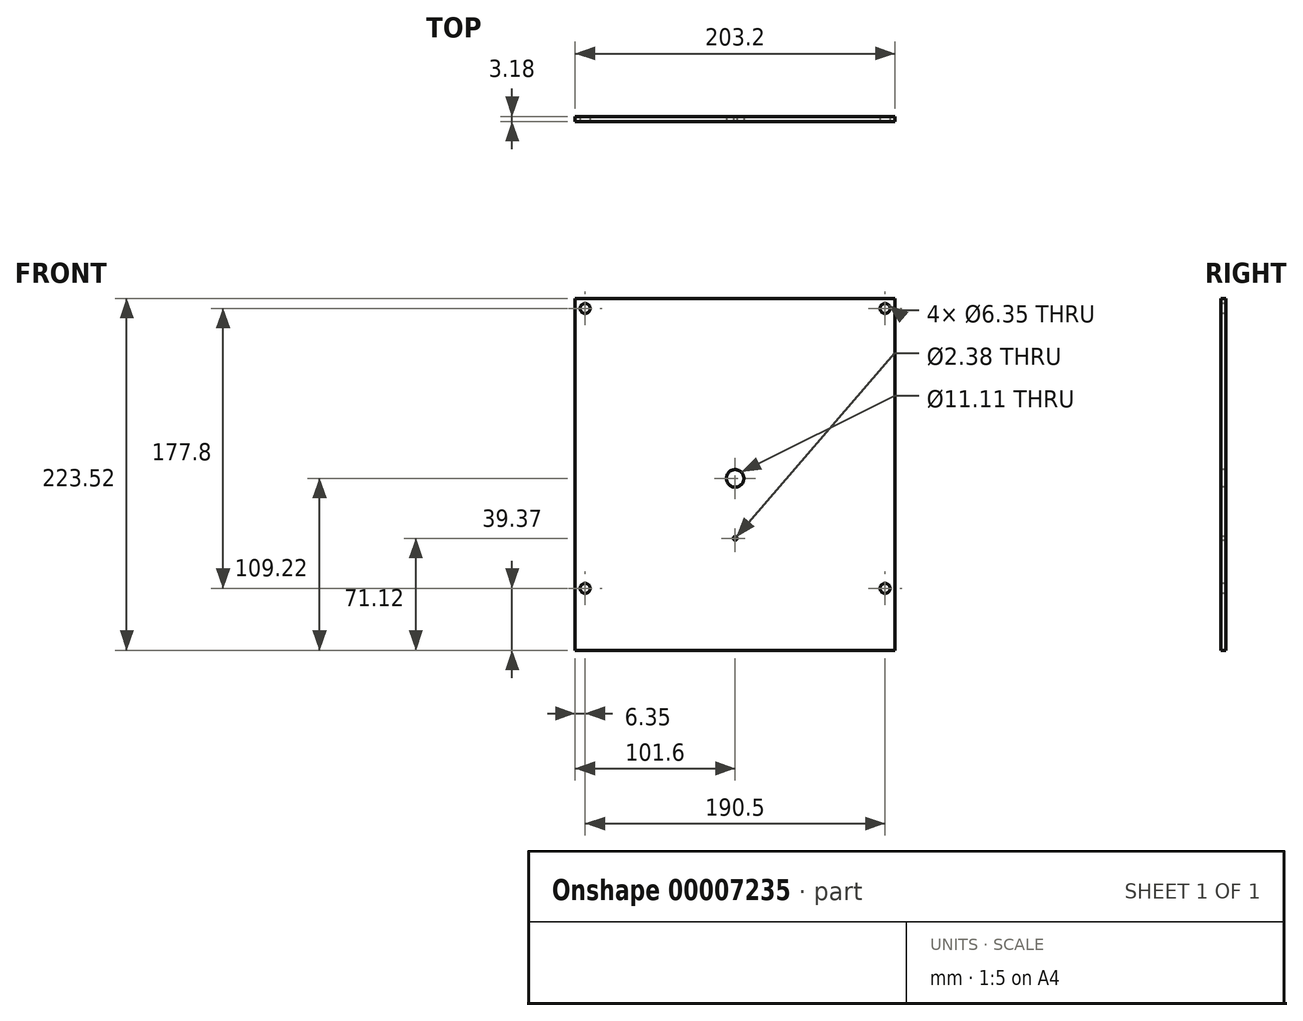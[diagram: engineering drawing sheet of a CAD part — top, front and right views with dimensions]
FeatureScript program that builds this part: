
annotation { "Feature Type Name" : "Feature", "Feature Type Description" : "" }
export const myFeature = defineFeature(function(context is Context, id is Id, definition is map)
    precondition{}
    {
        {
            var Q0;
            Q0=qCreatedBy(makeId("Front.planeOp"),FACE);
            var sketch = newSketch(context, id + "F0", { "sketchPlane" : qUnion([Q0])});
            skLineSegment(sketch, "E0.bottom", {"start": v(-101.6, 114.3) * mm, "end": v(101.6, 114.3) * mm});
            skLineSegment(sketch, "E0.top", {"start": v(-101.6, -109.22) * mm, "end": v(101.6, -109.22) * mm});
            skLineSegment(sketch, "E0.left", {"start": v(-101.6, 114.3) * mm, "end": v(-101.6, -109.22) * mm});
            skLineSegment(sketch, "E0.right", {"start": v(101.6, 114.3) * mm, "end": v(101.6, -109.22) * mm});
            skLineSegment(sketch, "E1", {"start": v(0, -109.22) * mm, "end": v(0, 114.3) * mm, "construction": true});
            skSolve(sketch);
        }
        {
            var Q0;
            Q0=qSketchRegion(id+"F0",true);
            extrude(context, id + "F1", {"entities" : qUnion([Q0]), "oppositeDirection" : true, "depth" : 3.17 * mm});
        }
        {
            var Q0;
            Q0=makeQuery(id+"F1.opExtrude","CAP_FACE",FACE,{"disambiguationData":[OSD([sQuery(id+"F0.wireOp",EDGE,"E0.bottom"),sQuery(id+"F0.wireOp",EDGE,"E0.top"),sQuery(id+"F0.wireOp",EDGE,"E0.left"),sQuery(id+"F0.wireOp",EDGE,"E0.right")])],"isStart":true});
            var sketch = newSketch(context, id + "F2", { "sketchPlane" : qUnion([Q0])});
            skCircle(sketch, "E2", {"center": v(0, 0) * mm, "radius": 5.56 * mm});
            skCircle(sketch, "E3", {"center": v(0, -38.1) * mm, "radius": 1.2 * mm});
            skSolve(sketch);
        }
        {
            var Q0;
            Q0=qSketchRegion(id+"F2",true);
            extrude(context, id + "F3", {"entities" : qUnion([Q0]), "operationType" : NewBodyOperationType.REMOVE, "oppositeDirection" : true, "depth" : 25.4 * mm});
        }
        {
            var Q0;
            Q0=makeQuery(id+"F1.opExtrude","CAP_FACE",FACE,{"disambiguationData":[OSD([sQuery(id+"F0.wireOp",EDGE,"E0.bottom"),sQuery(id+"F0.wireOp",EDGE,"E0.top"),sQuery(id+"F0.wireOp",EDGE,"E0.left"),sQuery(id+"F0.wireOp",EDGE,"E0.right")])],"isStart":true});
            var sketch = newSketch(context, id + "F4", { "sketchPlane" : qUnion([Q0])});
            skCircle(sketch, "E4", {"center": v(-95.25, 107.95) * mm, "radius": 3.18 * mm});
            skCircle(sketch, "E5", {"center": v(95.25, 107.95) * mm, "radius": 3.18 * mm});
            skCircle(sketch, "E6", {"center": v(95.25, -69.85) * mm, "radius": 3.18 * mm});
            skCircle(sketch, "E7", {"center": v(-95.25, -69.85) * mm, "radius": 3.18 * mm});
            skSolve(sketch);
        }
        {
            var Q0;
            Q0=qSketchRegion(id+"F4",true);
            extrude(context, id + "F5", {"entities" : qUnion([Q0]), "operationType" : NewBodyOperationType.REMOVE, "endBound" : BoundingType.UP_TO_NEXT, "oppositeDirection" : true, "depth" : 25.4 * mm});
        }
    });
